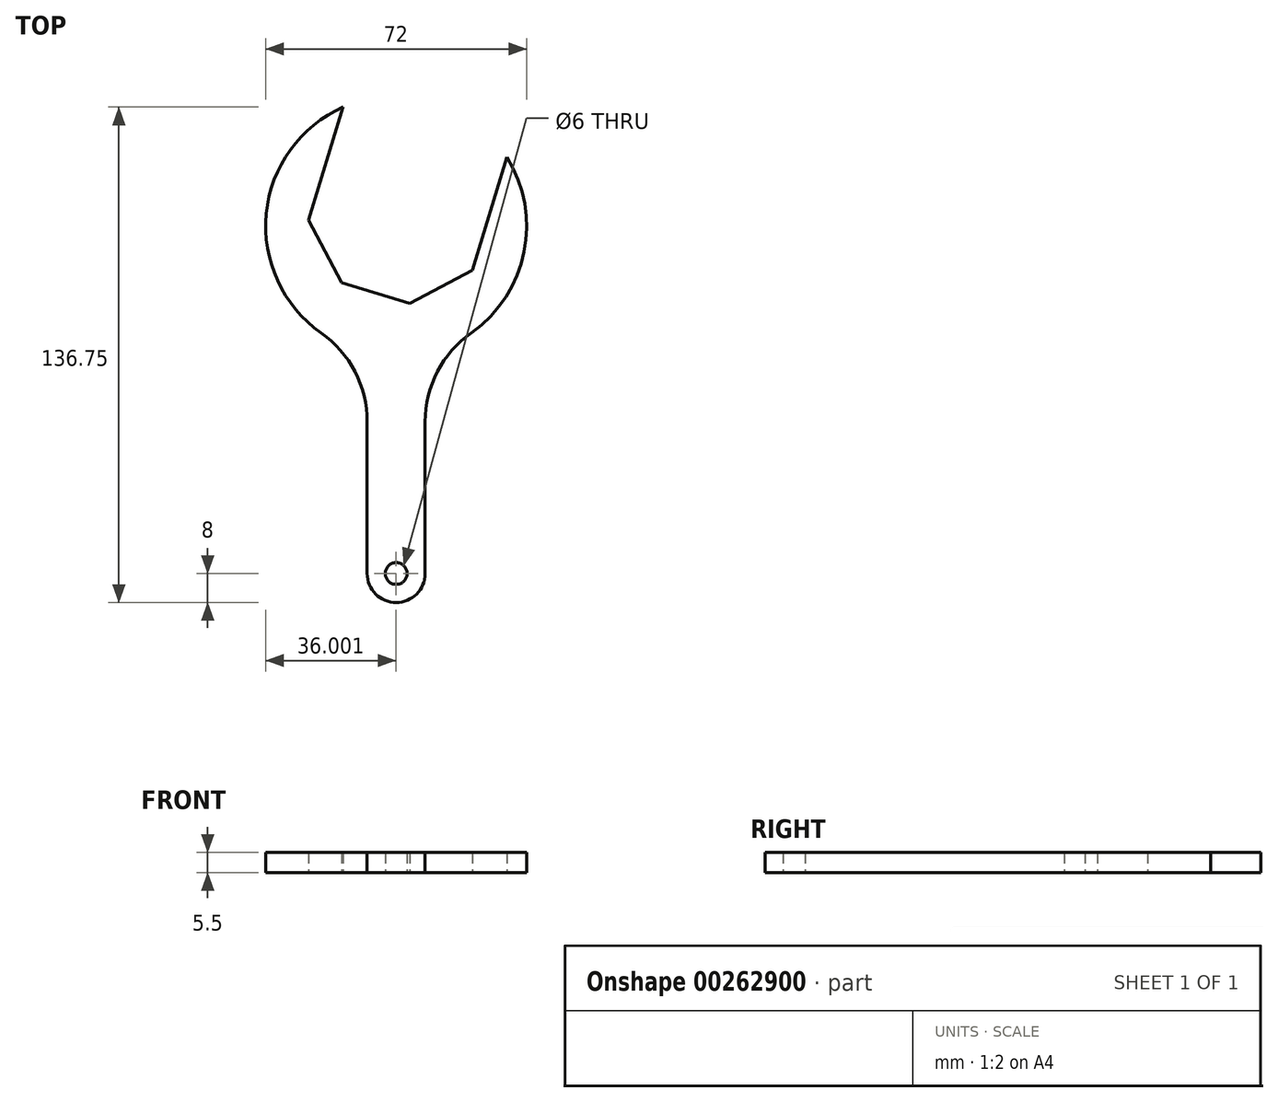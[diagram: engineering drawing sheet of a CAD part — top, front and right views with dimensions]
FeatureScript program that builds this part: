
annotation { "Feature Type Name" : "Feature", "Feature Type Description" : "" }
export const myFeature = defineFeature(function(context is Context, id is Id, definition is map)
    precondition{}
    {
        {
            var Q0;
            Q0=qCreatedBy(makeId("Top.planeOp"),FACE);
            var sketch = newSketch(context, id + "F0", { "sketchPlane" : qUnion([Q0])});
            skArc(sketch, "E0", {"start": v(-9.27, -100) * mm, "mid": v(-1.27, -108) * mm, "end": v(6.73, -100) * mm});
            skLineSegment(sketch, "E1.trimOffspring", {"start": v(6.73, -58.11) * mm, "end": v(6.73, -100) * mm});
            skLineSegment(sketch, "E2.trimOffspring", {"start": v(-9.27, -58.11) * mm, "end": v(-9.27, -100) * mm});
            skCircle(sketch, "E3", {"center": v(-1.27, -100) * mm, "radius": 3 * mm});
            skArc(sketch, "E4", {"start": v(19.46, -33.59) * mm, "mid": v(34.02, -11.27) * mm, "end": v(29.25, 14.95) * mm});
            skArc(sketch, "E5", {"start": v(-9.27, -39.25) * mm, "mid": v(-1.27, -40.15) * mm, "end": v(6.73, -39.25) * mm, "construction": true});
            skLineSegment(sketch, "E6", {"start": v(-1.27, -4.15) * mm, "end": v(-1.27, -100) * mm, "construction": true});
            skLineSegment(sketch, "E7", {"start": v(-15.5, 28.92) * mm, "end": v(-15.5, 28.92) * mm});
            skArc(sketch, "E8", {"start": v(-15.89, 28.75) * mm, "mid": v(-37.1, -0.64) * mm, "end": v(-22, -33.59) * mm});
            skArc(sketch, "E9", {"start": v(29.25, 14.95) * mm, "mid": v(9.26, 30.28) * mm, "end": v(-15.89, 28.75) * mm, "construction": true});
            skPoint(sketch, "E10.visualSharp", {"position": v(6.73, -39.25) * mm});
            skArc(sketch, "E10.filletArc", {"start": v(19.46, -33.59) * mm, "mid": v(10.1, -44.3) * mm, "end": v(6.73, -58.11) * mm});
            skPoint(sketch, "E11.visualSharp", {"position": v(-9.27, -39.25) * mm});
            skArc(sketch, "E11.filletArc", {"start": v(-9.27, -58.11) * mm, "mid": v(-12.64, -44.3) * mm, "end": v(-22, -33.59) * mm});
            skCircle(sketch, "E12.cCircle", {"center": v(0, 0) * mm, "radius": 23.6 * mm, "construction": true});
            skLineSegment(sketch, "E12.0", {"start": v(16.25, 19.71) * mm, "end": v(25.43, 2.45) * mm, "construction": true});
            skLineSegment(sketch, "E12.1", {"start": v(29.25, 14.95) * mm, "end": v(19.71, -16.25) * mm});
            skLineSegment(sketch, "E12.2", {"start": v(19.71, -16.25) * mm, "end": v(2.45, -25.43) * mm});
            skLineSegment(sketch, "E12.3", {"start": v(2.45, -25.43) * mm, "end": v(-16.25, -19.71) * mm});
            skLineSegment(sketch, "E12.4", {"start": v(-16.25, -19.71) * mm, "end": v(-25.43, -2.45) * mm});
            skLineSegment(sketch, "E12.5", {"start": v(-25.43, -2.45) * mm, "end": v(-15.89, 28.75) * mm});
            skLineSegment(sketch, "E12.6", {"start": v(-19.71, 16.25) * mm, "end": v(-2.45, 25.43) * mm, "construction": true});
            skLineSegment(sketch, "E12.7", {"start": v(-2.45, 25.43) * mm, "end": v(16.25, 19.71) * mm, "construction": true});
            skPoint(sketch, "E12.0.midPoint", {"position": v(20.84, 11.08) * mm});
            skLineSegment(sketch, "E13", {"start": v(0, 0) * mm, "end": v(-6.9, -22.57) * mm, "construction": true});
            skSolve(sketch);
        }
        {
            var Q0;
            Q0=qSketchRegion(id+"F0",true);
            extrude(context, id + "F1", {"entities" : qUnion([Q0]), "depth" : 5.5 * mm});
        }
    });
